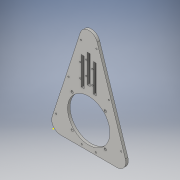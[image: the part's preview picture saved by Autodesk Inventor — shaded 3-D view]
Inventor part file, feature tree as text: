
AUTODESK INVENTOR PART (.ipt)
format: ipt  version: 2016 (Build 200138000, 138)  size: 214,016 bytes
history: native  units: in
note: dims shown in document units (in); Inventor stores cm internally (conversion verified against a paired STEP export)
features: sketch x3, extrude x3
ambient origin geometry x8: Origin, YZ Plane, XZ Plane, XY Plane, X Axis, Y Axis, Z Axis, Center Point
bodies: Body1 (feature_tree)
feature tree (6):
  sketch  "Sketch1"  dims[d12=0.25in d13=3.0in d14=0.166in d15=0.166in d16=0.166in d17=0.166in d18=0.15in d19=0.75in d20=0.75in d21=1.9in d22=1.9in d25=1.25in]
  extrude  "Extrusion3"  Depth=1.25in
  extrude  "Extrusion11"  Depth=1.25in
  sketch  "Sketch3"  dims[d30=1.0in d31=1.0in d32=1.0in d33=0.4in d34=0.4in d35=0.05in d37=0.05in d38=0.18in d39=0.0in d40=0.4in d41=0.4in d42=0.1in d43=0.1in d44=0.1in d45=0.1in d183=0.2in d184=2.0in d185=0.143in d186=0.22in d189=0.105in d194=0.2in d196=0.143in d197=0.22in d198=2.0in d199=0.0713in d203=0.105in d204=0.105in d205=0.0713in d207=1.643in d208=0.643in d209=0.0713in d211=0.2in d212=2.0in d216=0.105in d217=0.105in d218=0.18in d219=0.0in d221=0.175in d222=0.2in d224=0.2in d225=0.15in d226=0.18in d227=0.0in d228=1.5in d229=1.5in]
  extrude  "Extrusion12"  Depth=1.5in
  sketch  "Sketch2"  dims[d26=1.25in d27=1.25in]
